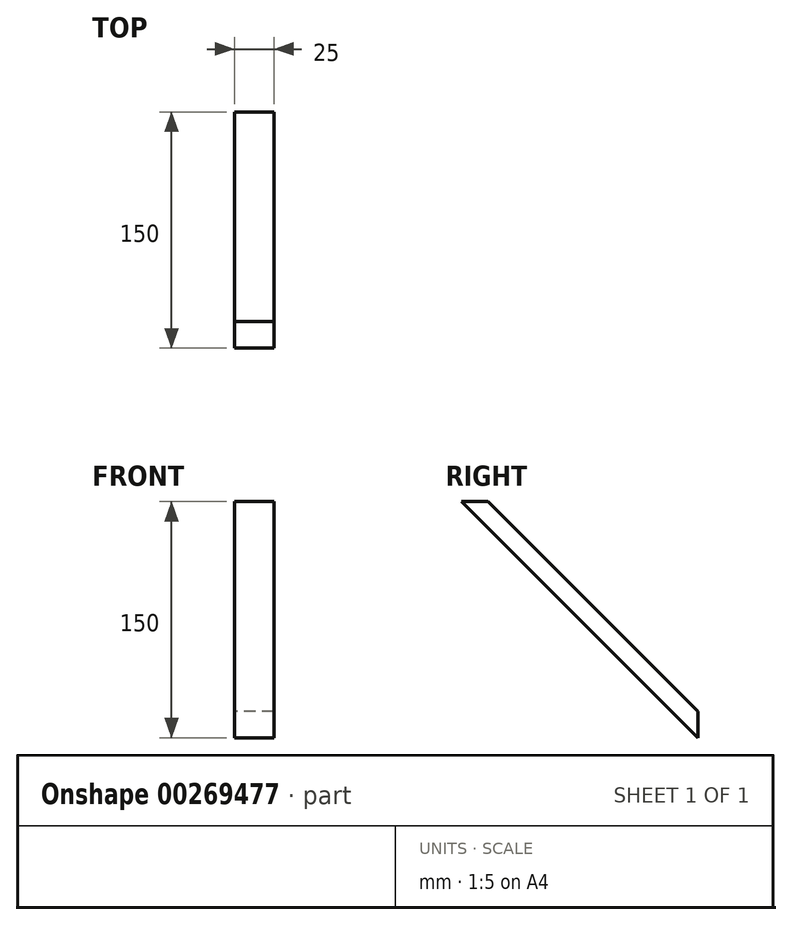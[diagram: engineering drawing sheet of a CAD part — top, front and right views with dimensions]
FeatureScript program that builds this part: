
annotation { "Feature Type Name" : "Feature", "Feature Type Description" : "" }
export const myFeature = defineFeature(function(context is Context, id is Id, definition is map)
    precondition{}
    {
        {
            var Q0;
            Q0=qCreatedBy(makeId("Right.planeOp"),FACE);
            var sketch = newSketch(context, id + "F0", { "sketchPlane" : qUnion([Q0])});
            skLineSegment(sketch, "E0.bottom", {"start": v(-73.73, 10) * mm, "end": v(76.27, 10) * mm});
            skLineSegment(sketch, "E0.top", {"start": v(-73.73, -140) * mm, "end": v(76.27, -140) * mm});
            skLineSegment(sketch, "E0.left", {"start": v(-73.73, 10) * mm, "end": v(-73.73, -140) * mm});
            skLineSegment(sketch, "E0.right", {"start": v(76.27, 10) * mm, "end": v(76.27, -140) * mm});
            skLineSegment(sketch, "E1.top", {"start": v(-73.73, 0) * mm, "end": v(76.27, 0) * mm});
            skLineSegment(sketch, "E1.left", {"start": v(-73.73, 10) * mm, "end": v(-73.73, 0) * mm});
            skLineSegment(sketch, "E1.right", {"start": v(76.27, 10) * mm, "end": v(76.27, 0) * mm});
            skLineSegment(sketch, "E2.bottom", {"start": v(76.27, -140) * mm, "end": v(66.27, -140) * mm});
            skLineSegment(sketch, "E2.top", {"start": v(76.27, 0) * mm, "end": v(66.27, 0) * mm});
            skLineSegment(sketch, "E2.left", {"start": v(76.27, -140) * mm, "end": v(76.27, 0) * mm});
            skLineSegment(sketch, "E2.right", {"start": v(66.27, -140) * mm, "end": v(66.27, 0) * mm});
            skLineSegment(sketch, "E3", {"start": v(-73.73, 10) * mm, "end": v(76.27, -140) * mm});
            skLineSegment(sketch, "E4", {"start": v(-57.03, 10) * mm, "end": v(76.27, -123.3) * mm});
            skSolve(sketch);
        }
        {
            var Q0;
            {var subQ0=sQuery(id+"F0.wireOp",EDGE,"E3");var subQ5=sQuery(id+"F0.wireOp",EDGE,"E1.top");var subQ6=makeQuery(id+"F0.imprint","INTERSECT",VERTEX,{"derivedFrom":[subQ5,subQ0]});Q0=makeQuery(id+"F0.imprint","IMPRINT",FACE,{"disambiguationData":[TD([[makeQuery(id+"F0.imprint","IMPRINT",EDGE,{"disambiguationData":[TD([[subQ6,-1.0]])],"derivedFrom":subQ5}),1.0]])]});}
            var Q1;
            {var subQ1=sQuery(id+"F0.wireOp",EDGE,"E1.right");Q1=makeQuery(id+"F0.imprint","IMPRINT",FACE,{"disambiguationData":[TD([[makeQuery(id+"F0.imprint","IMPRINT",EDGE,{"derivedFrom":subQ1}),-1.0]])]});}
            var Q2;
            {var subQ0=sQuery(id+"F0.wireOp",EDGE,"E2.top");Q2=makeQuery(id+"F0.imprint","IMPRINT",FACE,{"disambiguationData":[TD([[makeQuery(id+"F0.imprint","IMPRINT",EDGE,{"derivedFrom":subQ0}),1.0]])]});}
            var Q3;
            {var subQ0=sQuery(id+"F0.wireOp",EDGE,"E3");var subQ5=sQuery(id+"F0.wireOp",EDGE,"E2.right");var subQ6=makeQuery(id+"F0.imprint","INTERSECT",VERTEX,{"derivedFrom":[subQ5,subQ0]});Q3=makeQuery(id+"F0.imprint","IMPRINT",FACE,{"disambiguationData":[TD([[makeQuery(id+"F0.imprint","IMPRINT",EDGE,{"disambiguationData":[TD([[subQ6,-1.0]])],"derivedFrom":subQ5}),-1.0]])]});}
            var Q4;
            {var subQ0=sQuery(id+"F0.wireOp",EDGE,"E3");var subQ1=sQuery(id+"F0.wireOp",EDGE,"E1.top");var subQ2=makeQuery(id+"F0.imprint","INTERSECT",VERTEX,{"derivedFrom":[subQ1,subQ0]});Q4=makeQuery(id+"F0.imprint","IMPRINT",FACE,{"disambiguationData":[TD([[makeQuery(id+"F0.imprint","IMPRINT",EDGE,{"disambiguationData":[TD([[subQ2,-1.0]])],"derivedFrom":subQ1}),-1.0]])]});}
            extrude(context, id + "F1", {"entities" : qUnion([Q0, Q1, Q2, Q3, Q4]), "depth" : 25 * mm});
        }
    });
